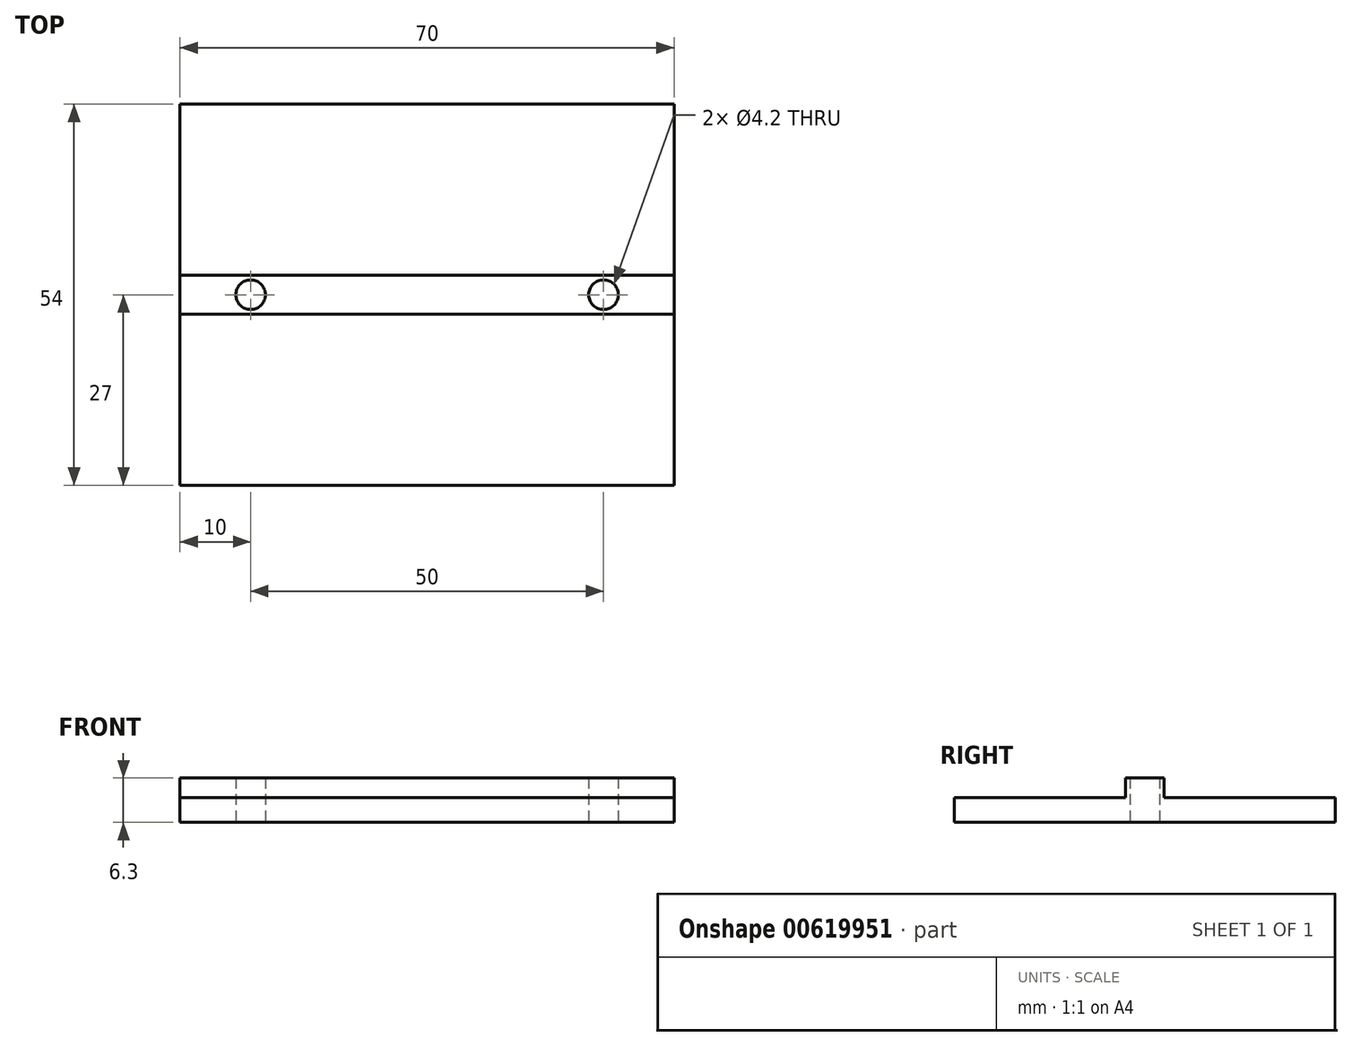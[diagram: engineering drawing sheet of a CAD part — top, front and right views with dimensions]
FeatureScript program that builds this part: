
annotation { "Feature Type Name" : "Feature", "Feature Type Description" : "" }
export const myFeature = defineFeature(function(context is Context, id is Id, definition is map)
    precondition{}
    {
        {
            var Q0;
            Q0=qCreatedBy(makeId("Right.planeOp"),FACE);
            var sketch = newSketch(context, id + "F0", { "sketchPlane" : qUnion([Q0])});
            skLineSegment(sketch, "E0.bottom", {"start": v(27, 1.75) * mm, "end": v(-27, 1.75) * mm});
            skLineSegment(sketch, "E0.top", {"start": v(27, -1.75) * mm, "end": v(-27, -1.75) * mm});
            skLineSegment(sketch, "E0.left", {"start": v(27, 1.75) * mm, "end": v(27, -1.75) * mm});
            skLineSegment(sketch, "E0.right", {"start": v(-27, 1.75) * mm, "end": v(-27, -1.75) * mm});
            skPoint(sketch, "E0.middle", {"position": v(0, 0) * mm});
            skPoint(sketch, "E1", {"position": v(0, 1.75) * mm});
            skPoint(sketch, "E2", {"position": v(0, 3.15) * mm});
            skLineSegment(sketch, "E3.bottom", {"start": v(2.75, 4.55) * mm, "end": v(-2.75, 4.55) * mm});
            skLineSegment(sketch, "E3.top", {"start": v(2.75, 1.75) * mm, "end": v(-2.75, 1.75) * mm});
            skLineSegment(sketch, "E3.left", {"start": v(2.75, 4.55) * mm, "end": v(2.75, 1.75) * mm});
            skLineSegment(sketch, "E3.right", {"start": v(-2.75, 4.55) * mm, "end": v(-2.75, 1.75) * mm});
            skSolve(sketch);
        }
        {
            var Q0;
            Q0=makeQuery(id+"F0.imprint","IMPRINT",FACE,{"disambiguationData":[TD([[makeQuery(id+"F0.imprint","IMPRINT",EDGE,{"derivedFrom":sQuery(id+"F0.wireOp",EDGE,"E0.bottom")}),1.0]])]});
            var Q1;
            Q1=makeQuery(id+"F0.imprint","IMPRINT",FACE,{"disambiguationData":[TD([[makeQuery(id+"F0.imprint","IMPRINT",EDGE,{"derivedFrom":sQuery(id+"F0.wireOp",EDGE,"E3.bottom")}),1.0]])]});
            extrude(context, id + "F1", {"entities" : qUnion([Q0, Q1]), "depth" : 70 * mm, "offsetDistance" : 25 * mm});
        }
        {
            var Q0;
            Q0=makeQuery(id+"F1.opExtrude","SWEPT_FACE",FACE,{"disambiguationData":[OSD([sQuery(id+"F0.wireOp",EDGE,"E3.bottom")])]});
            var sketch = newSketch(context, id + "F2", { "sketchPlane" : qUnion([Q0])});
            skPoint(sketch, "E4", {"position": v(10, 0) * mm});
            skPoint(sketch, "E5", {"position": v(35, 0) * mm});
            skPoint(sketch, "E5.positionSnap0", {"position": v(35, 2.75) * mm});
            skLineSegment(sketch, "E6", {"start": v(35, -27.03) * mm, "end": v(35, 27.03) * mm, "construction": true});
            skPoint(sketch, "E7.MirrorP", {"position": v(60, 0) * mm});
            skSolve(sketch);
        }
        {
            var Q0;
            Q0=sQuery(id+"F2.wireOp",VERTEX,"E4");
            var Q1;
            Q1=sQuery(id+"F2.wireOp",VERTEX,"E7.MirrorP");
            var Q2;
            Q2=makeQuery(id+"F1.opExtrude","SWEPT_BODY",BODY,{"disambiguationData":[OSD([sQuery(id+"F0.wireOp",EDGE,"E0.bottom"),sQuery(id+"F0.wireOp",EDGE,"E0.top"),sQuery(id+"F0.wireOp",EDGE,"E0.left"),sQuery(id+"F0.wireOp",EDGE,"E0.right"),sQuery(id+"F0.wireOp",EDGE,"E3.bottom"),sQuery(id+"F0.wireOp",EDGE,"E3.left"),sQuery(id+"F0.wireOp",EDGE,"E3.right")])]});
            hole(context, id + "F3", {"style" : HoleStyle.SIMPLE, "endStyle" : HoleEndStyle.THROUGH, "standardTappedOrClearance" : lookupTablePath({ "standard" : "ISO", "engagement" : "75%", "pitch" : "0.8 mm", "size" : "M5", "type" : "Tapped" }), "standardBlindInLast" : lookupTablePath({ "standard" : "ISO", "engagement" : "75%", "pitch" : "0.8 mm", "size" : "M5", "type" : "Tapped" }), "holeDiameter" : 4.2 * mm, "majorDiameter" : 5 * mm, "showTappedDepth" : true, "isTappedThrough" : true, "tappedDepth" : 7.6 * mm, "tapClearance" : 3, "locations" : qUnion([Q0, Q1]), "scope" : qUnion([Q2]), "startStyle" : HoleStartStyle.SKETCH});
        }
    });
